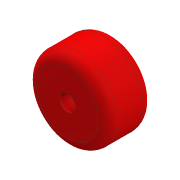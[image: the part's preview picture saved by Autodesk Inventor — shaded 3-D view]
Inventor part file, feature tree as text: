
AUTODESK INVENTOR PART (.ipt)
format: ipt  version: 2020 (Build 240168000, 168)  size: 135,680 bytes
history: native  units: mm
features: other x1, extrude x1, fillet x1, sketch x1
ambient origin geometry x8: Origin, YZ Plane, XZ Plane, XY Plane, X Axis, Y Axis, Z Axis, Center Point
bodies: Body1 (feature_tree)
feature tree (4):
  other  "솔리드1"
  extrude  "돌출1"  Depth=25.0mm
  fillet  "모깎기1"  Radius=5.0mm
  sketch  "스케치1"
